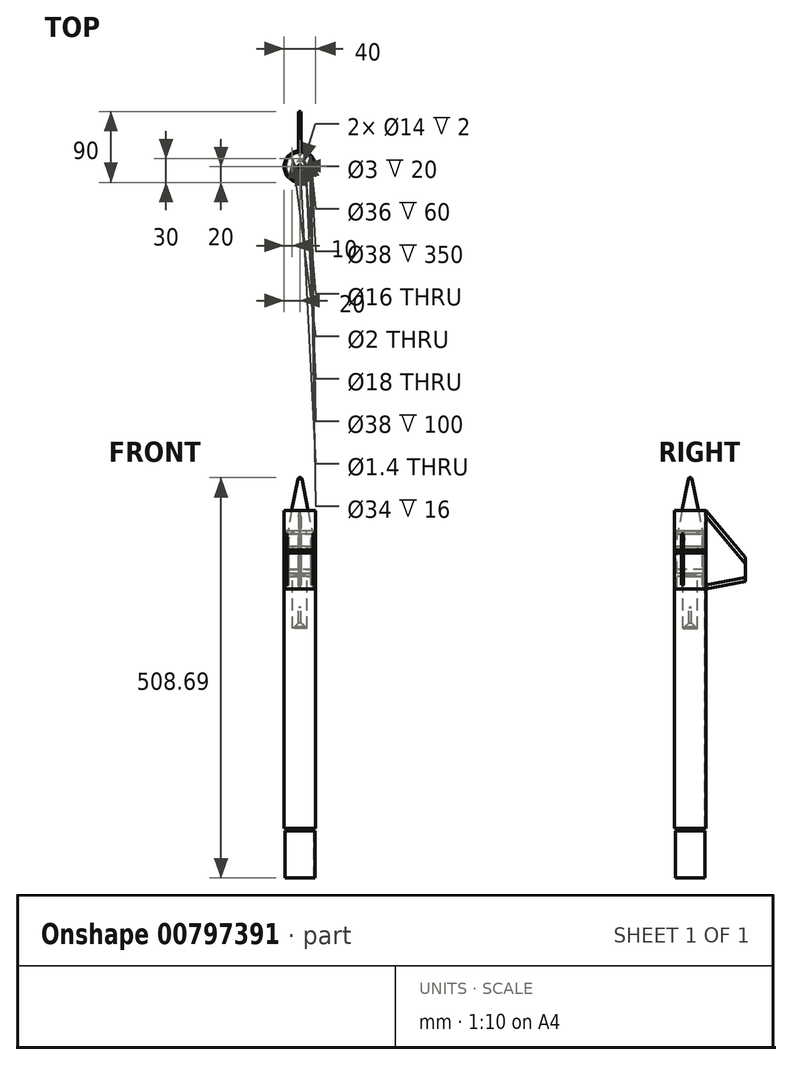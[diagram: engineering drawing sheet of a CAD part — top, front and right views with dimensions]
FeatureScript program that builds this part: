
annotation { "Feature Type Name" : "Feature", "Feature Type Description" : "" }
export const myFeature = defineFeature(function(context is Context, id is Id, definition is map)
    precondition{}
    {
        {
            var Q0;
            Q0=qCreatedBy(makeId("Front.planeOp"),FACE);
            var sketch = newSketch(context, id + "F0", { "sketchPlane" : qUnion([Q0])});
            skLineSegment(sketch, "E0", {"start": v(0, -25) * mm, "end": v(19, -25) * mm});
            skLineSegment(sketch, "E1", {"start": v(19, -25) * mm, "end": v(19, 0) * mm});
            skLineSegment(sketch, "E2", {"start": v(19, 0) * mm, "end": v(20, 0) * mm});
            skLineSegment(sketch, "E3", {"start": v(20, 0) * mm, "end": v(2.5, 90) * mm});
            skLineSegment(sketch, "E4", {"start": v(0, -25) * mm, "end": v(0, 89) * mm, "construction": true});
            skArc(sketch, "E5", {"start": v(2.5, 90) * mm, "mid": v(1.5, 91.23) * mm, "end": v(0, 91.7) * mm});
            skLineSegment(sketch, "E6", {"start": v(0, 91.7) * mm, "end": v(0, -25) * mm});
            skSolve(sketch);
        }
        {
            var Q0;
            Q0=makeQuery(id+"F0.imprint","IMPRINT",FACE,{"disambiguationData":[TD([[makeQuery(id+"F0.imprint","IMPRINT",EDGE,{"derivedFrom":sQuery(id+"F0.wireOp",EDGE,"E0")}),1.0]])]});
            var Q1;
            Q1=sQuery(id+"F0.wireOp",EDGE,"E6");
            revolve(context, id + "F1", {"surfaceOperationType" : NewSurfaceOperationType.NEW, "entities" : qUnion([Q0]), "axis" : qUnion([Q1]), "revolveType" : RevolveType.FULL});
        }
        {
            var Q0;
            Q0=qCreatedBy(makeId("Front.planeOp"),FACE);
            var sketch = newSketch(context, id + "F2", { "sketchPlane" : qUnion([Q0])});
            skLineSegment(sketch, "E7.bottom", {"start": v(19, -4) * mm, "end": v(20, -4) * mm});
            skLineSegment(sketch, "E7.top", {"start": v(19, -354) * mm, "end": v(20, -354) * mm});
            skLineSegment(sketch, "E7.left", {"start": v(19, -4) * mm, "end": v(19, -354) * mm});
            skLineSegment(sketch, "E7.right", {"start": v(20, -4) * mm, "end": v(20, -354) * mm});
            skLineSegment(sketch, "E8", {"start": v(0, 0) * mm, "end": v(0, -354) * mm, "construction": true});
            skSolve(sketch);
        }
        {
            var Q0;
            Q0=makeQuery(id+"F2.imprint","IMPRINT",FACE,{"disambiguationData":[TD([[makeQuery(id+"F2.imprint","IMPRINT",EDGE,{"derivedFrom":sQuery(id+"F2.wireOp",EDGE,"E7.bottom")}),-1.0]])]});
            var Q1;
            Q1=sQuery(id+"F2.wireOp",EDGE,"E8");
            revolve(context, id + "F3", {"surfaceOperationType" : NewSurfaceOperationType.NEW, "entities" : qUnion([Q0]), "axis" : qUnion([Q1]), "revolveType" : RevolveType.FULL});
        }
        {
            var Q0;
            Q0=qCreatedBy(makeId("Front.planeOp"),FACE);
            var sketch = newSketch(context, id + "F4", { "sketchPlane" : qUnion([Q0])});
            skLineSegment(sketch, "E9.bottom", {"start": v(18, -357) * mm, "end": v(19, -357) * mm});
            skLineSegment(sketch, "E9.top", {"start": v(18, -417) * mm, "end": v(19, -417) * mm});
            skLineSegment(sketch, "E9.left", {"start": v(18, -357) * mm, "end": v(18, -417) * mm});
            skLineSegment(sketch, "E9.right", {"start": v(19, -357) * mm, "end": v(19, -417) * mm});
            skLineSegment(sketch, "E10", {"start": v(0, 0) * mm, "end": v(0, -683.2) * mm, "construction": true});
            skSolve(sketch);
        }
        {
            var Q0;
            Q0=makeQuery(id+"F4.imprint","IMPRINT",FACE,{"disambiguationData":[TD([[makeQuery(id+"F4.imprint","IMPRINT",EDGE,{"derivedFrom":sQuery(id+"F4.wireOp",EDGE,"E9.bottom")}),-1.0]])]});
            var Q1;
            Q1=sQuery(id+"F4.wireOp",EDGE,"E10");
            revolve(context, id + "F5", {"surfaceOperationType" : NewSurfaceOperationType.NEW, "entities" : qUnion([Q0]), "axis" : qUnion([Q1]), "revolveType" : RevolveType.FULL});
        }
        {
            var Q0;
            Q0=qCreatedBy(makeId("Front.planeOp"),FACE);
            var sketch = newSketch(context, id + "F6", { "sketchPlane" : qUnion([Q0])});
            skLineSegment(sketch, "E11", {"start": v(0, 0) * mm, "end": v(0, -100) * mm, "construction": true});
            skLineSegment(sketch, "E12", {"start": v(17, 0) * mm, "end": v(18, 0) * mm});
            skLineSegment(sketch, "E13", {"start": v(18, 0) * mm, "end": v(18, -50) * mm});
            skLineSegment(sketch, "E14", {"start": v(18, -50) * mm, "end": v(17, -50) * mm});
            skLineSegment(sketch, "E15", {"start": v(17, -50) * mm, "end": v(17, -34) * mm});
            skLineSegment(sketch, "E16", {"start": v(17, -34) * mm, "end": v(0.7, -34) * mm});
            skLineSegment(sketch, "E17", {"start": v(0.7, -34) * mm, "end": v(0.7, -30) * mm});
            skLineSegment(sketch, "E18", {"start": v(0.7, -30) * mm, "end": v(17, -30) * mm});
            skLineSegment(sketch, "E19", {"start": v(17, -30) * mm, "end": v(17, 0) * mm});
            skSolve(sketch);
        }
        {
            var Q0;
            Q0=makeQuery(id+"F6.imprint","IMPRINT",FACE,{"disambiguationData":[TD([[makeQuery(id+"F6.imprint","IMPRINT",EDGE,{"derivedFrom":sQuery(id+"F6.wireOp",EDGE,"E12")}),-1.0]])]});
            var Q1;
            Q1=sQuery(id+"F6.wireOp",EDGE,"E11");
            revolve(context, id + "F7", {"surfaceOperationType" : NewSurfaceOperationType.NEW, "entities" : qUnion([Q0]), "axis" : qUnion([Q1]), "revolveType" : RevolveType.FULL});
        }
        {
            var Q0;
            Q0=qCreatedBy(makeId("Front.planeOp"),FACE);
            var sketch = newSketch(context, id + "F8", { "sketchPlane" : qUnion([Q0])});
            skLineSegment(sketch, "E20.bottom", {"start": v(20, 50) * mm, "end": v(19, 50) * mm});
            skLineSegment(sketch, "E20.top", {"start": v(20, -50) * mm, "end": v(19, -50) * mm});
            skLineSegment(sketch, "E20.left", {"start": v(20, 50) * mm, "end": v(20, -50) * mm});
            skLineSegment(sketch, "E20.right", {"start": v(19, 50) * mm, "end": v(19, -50) * mm});
            skLineSegment(sketch, "E21", {"start": v(0, 55) * mm, "end": v(0, -55) * mm, "construction": true});
            skSolve(sketch);
        }
        {
            var Q0;
            Q0=makeQuery(id+"F8.imprint","IMPRINT",FACE,{"disambiguationData":[TD([[makeQuery(id+"F8.imprint","IMPRINT",EDGE,{"derivedFrom":sQuery(id+"F8.wireOp",EDGE,"E20.bottom")}),1.0]])]});
            var Q1;
            Q1=sQuery(id+"F8.wireOp",EDGE,"E21");
            revolve(context, id + "F9", {"surfaceOperationType" : NewSurfaceOperationType.NEW, "entities" : qUnion([Q0]), "axis" : qUnion([Q1]), "revolveType" : RevolveType.FULL});
        }
        {
            var Q0;
            Q0=qCreatedBy(makeId("Top.planeOp"),FACE);
            cPlane(context, id + "F10", {"entities" : qUnion([Q0]), "cplaneType" : CPlaneType.OFFSET, "offset" : 20 * mm, "width" : 150 * mm, "height" : 150 * mm});
        }
        {
            var Q0;
            Q0=qCreatedBy(id+"F10.planeOp",FACE);
            var sketch = newSketch(context, id + "F11", { "sketchPlane" : qUnion([Q0])});
            skLineSegment(sketch, "E22.bottom", {"start": v(-1.5, 21.95) * mm, "end": v(1.5, 21.95) * mm});
            skLineSegment(sketch, "E22.top", {"start": v(-1.5, 16.95) * mm, "end": v(1.5, 16.95) * mm});
            skLineSegment(sketch, "E22.left", {"start": v(-1.5, 21.95) * mm, "end": v(-1.5, 16.95) * mm});
            skLineSegment(sketch, "E22.right", {"start": v(1.5, 21.95) * mm, "end": v(1.5, 16.95) * mm});
            skLineSegment(sketch, "E23.1.0", {"start": v(-18.26, -12.27) * mm, "end": v(-19.76, -9.68) * mm});
            skLineSegment(sketch, "E23.1.1", {"start": v(-18.26, -12.27) * mm, "end": v(-13.93, -9.77) * mm});
            skLineSegment(sketch, "E23.2.0", {"start": v(19.76, -9.68) * mm, "end": v(18.26, -12.27) * mm});
            skLineSegment(sketch, "E23.2.1", {"start": v(19.76, -9.68) * mm, "end": v(15.43, -7.18) * mm});
            skPoint(sketch, "E23.center", {"position": v(0, 0) * mm});
            skLineSegment(sketch, "E24.1.0", {"start": v(-19.76, -9.68) * mm, "end": v(-15.43, -7.18) * mm});
            skLineSegment(sketch, "E24.1.1", {"start": v(-13.93, -9.77) * mm, "end": v(-15.43, -7.18) * mm});
            skLineSegment(sketch, "E24.2.0", {"start": v(18.26, -12.27) * mm, "end": v(13.93, -9.77) * mm});
            skLineSegment(sketch, "E24.2.1", {"start": v(15.43, -7.18) * mm, "end": v(13.93, -9.77) * mm});
            skSolve(sketch);
        }
        {
            var Q0;
            Q0=makeQuery(id+"F11.imprint","IMPRINT",FACE,{"disambiguationData":[TD([[makeQuery(id+"F11.imprint","IMPRINT",EDGE,{"derivedFrom":sQuery(id+"F11.wireOp",EDGE,"E24.1.0")}),-1.0]])]});
            var Q1;
            Q1=makeQuery(id+"F11.imprint","IMPRINT",FACE,{"disambiguationData":[TD([[makeQuery(id+"F11.imprint","IMPRINT",EDGE,{"derivedFrom":sQuery(id+"F11.wireOp",EDGE,"E24.2.0")}),-1.0]])]});
            var Q2;
            Q2=makeQuery(id+"F11.imprint","IMPRINT",FACE,{"disambiguationData":[TD([[makeQuery(id+"F11.imprint","IMPRINT",EDGE,{"derivedFrom":sQuery(id+"F11.wireOp",EDGE,"E22.bottom")}),-1.0]])]});
            extrude(context, id + "F12", {"entities" : qUnion([Q0, Q1, Q2]), "operationType" : NewBodyOperationType.REMOVE, "depth" : -65 * mm, "offsetDistance" : 25 * mm});
        }
        {
            var Q0;
            Q0=qCreatedBy(makeId("Right.planeOp"),FACE);
            var sketch = newSketch(context, id + "F13", { "sketchPlane" : qUnion([Q0])});
            skLineSegment(sketch, "E25", {"start": v(20, 50) * mm, "end": v(70, -10) * mm});
            skLineSegment(sketch, "E26", {"start": v(70, -10) * mm, "end": v(70, -40) * mm});
            skLineSegment(sketch, "E27", {"start": v(70, -40) * mm, "end": v(20, -50) * mm});
            skLineSegment(sketch, "E28", {"start": v(20, -50) * mm, "end": v(20, -45) * mm});
            skLineSegment(sketch, "E29", {"start": v(20, -45) * mm, "end": v(15, -45) * mm});
            skLineSegment(sketch, "E30", {"start": v(20, 50) * mm, "end": v(20, 16) * mm});
            skLineSegment(sketch, "E31", {"start": v(20, 16) * mm, "end": v(15, 16) * mm});
            skLineSegment(sketch, "E32", {"start": v(15, 16) * mm, "end": v(15, -45) * mm});
            skSolve(sketch);
        }
        {
            var Q0;
            Q0=makeQuery(id+"F13.imprint","IMPRINT",FACE,{"disambiguationData":[TD([[makeQuery(id+"F13.imprint","IMPRINT",EDGE,{"derivedFrom":sQuery(id+"F13.wireOp",EDGE,"E25")}),-1.0]])]});
            extrude(context, id + "F14", {"entities" : qUnion([Q0]), "endBound" : BoundingType.SYMMETRIC, "oppositeDirection" : true, "depth" : 3 * mm, "offsetDistance" : 25 * mm});
        }
        {
            var Q0;
            Q0=makeQuery(id+"F14.opExtrude","CAP_EDGE",EDGE,{"disambiguationData":[OSD([sQuery(id+"F13.wireOp",EDGE,"E25")])],"isStart":true});
            var Q1;
            Q1=makeQuery(id+"F14.opExtrude","CAP_EDGE",EDGE,{"disambiguationData":[OSD([sQuery(id+"F13.wireOp",EDGE,"E25")])],"isStart":false});
            var Q2;
            Q2=makeQuery(id+"F14.opExtrude","CAP_EDGE",EDGE,{"disambiguationData":[OSD([sQuery(id+"F13.wireOp",EDGE,"E27")])],"isStart":true});
            chamfer(context, id + "F15", {"entities" : qUnion([Q0, Q1, Q2]), "chamferType" : ChamferType.TWO_OFFSETS, "width1" : 1 * mm, "oppositeDirection" : false, "width2" : 5 * mm, "tangentPropagation" : true});
        }
        {
            var Q0;
            Q0=makeQuery(id+"F14.opExtrude","CAP_EDGE",EDGE,{"disambiguationData":[OSD([sQuery(id+"F13.wireOp",EDGE,"E27")])],"isStart":false});
            chamfer(context, id + "F16", {"entities" : qUnion([Q0]), "chamferType" : ChamferType.TWO_OFFSETS, "width1" : 5 * mm, "oppositeDirection" : false, "width2" : 1 * mm, "tangentPropagation" : true});
        }
        {
            var Q0;
            Q0=qCreatedBy(makeId("Top.planeOp"),FACE);
            var sketch = newSketch(context, id + "F17", { "sketchPlane" : qUnion([Q0])});
            skCircle(sketch, "E33", {"center": v(0, 0) * mm, "radius": 9 * mm});
            skCircle(sketch, "E34", {"center": v(0, 0) * mm, "radius": 19 * mm});
            skSolve(sketch);
        }
        {
            var Q0;
            Q0=makeQuery(id+"F17.imprint","IMPRINT",FACE,{"disambiguationData":[TD([[makeQuery(id+"F17.imprint","IMPRINT",EDGE,{"derivedFrom":sQuery(id+"F17.wireOp",EDGE,"E33")}),-1.0]])]});
            extrude(context, id + "F18", {"entities" : qUnion([Q0]), "depth" : 4 * mm, "offsetDistance" : 25 * mm});
        }
        {
            var Q0;
            Q0=qCreatedBy(id+"F10.planeOp",FACE);
            var sketch = newSketch(context, id + "F19", { "sketchPlane" : qUnion([Q0])});
            skCircle(sketch, "E35", {"center": v(0, 0) * mm, "radius": 19 * mm});
            skCircle(sketch, "E36", {"center": v(0, 0) * mm, "radius": 8 * mm});
            skCircle(sketch, "E37", {"center": v(-10, 10) * mm, "radius": 1 * mm});
            skSolve(sketch);
        }
        {
            var Q0;
            Q0=makeQuery(id+"F19.imprint","IMPRINT",FACE,{"disambiguationData":[TD([[makeQuery(id+"F19.imprint","IMPRINT",EDGE,{"derivedFrom":sQuery(id+"F19.wireOp",EDGE,"E35")}),1.0]])]});
            extrude(context, id + "F20", {"entities" : qUnion([Q0]), "depth" : 4 * mm, "offsetDistance" : 25 * mm});
        }
        {
            var Q0;
            Q0=qCreatedBy(makeId("Front.planeOp"),FACE);
            var sketch = newSketch(context, id + "F21", { "sketchPlane" : qUnion([Q0])});
            skLineSegment(sketch, "E38", {"start": v(0, -32) * mm, "end": v(7, -32) * mm});
            skLineSegment(sketch, "E39", {"start": v(7, -32) * mm, "end": v(7, -30) * mm});
            skLineSegment(sketch, "E40", {"start": v(7, -30) * mm, "end": v(9, -30) * mm});
            skLineSegment(sketch, "E41", {"start": v(9, -30) * mm, "end": v(9, -100) * mm});
            skLineSegment(sketch, "E42", {"start": v(9, -100) * mm, "end": v(7, -100) * mm});
            skLineSegment(sketch, "E43", {"start": v(7, -100) * mm, "end": v(7, -98) * mm});
            skLineSegment(sketch, "E44", {"start": v(7, -98) * mm, "end": v(1.5, -93) * mm});
            skLineSegment(sketch, "E45", {"start": v(1.5, -93) * mm, "end": v(1.5, -73) * mm});
            skLineSegment(sketch, "E46", {"start": v(1.5, -73) * mm, "end": v(0, -73) * mm});
            skLineSegment(sketch, "E47", {"start": v(0, -73) * mm, "end": v(0, -32) * mm});
            skLineSegment(sketch, "E48", {"start": v(0, 0) * mm, "end": v(0, -130) * mm, "construction": true});
            skSolve(sketch);
        }
        {
            var Q0;
            Q0=makeQuery(id+"F21.imprint","IMPRINT",FACE,{"disambiguationData":[TD([[makeQuery(id+"F21.imprint","IMPRINT",EDGE,{"derivedFrom":sQuery(id+"F21.wireOp",EDGE,"E38")}),-1.0]])]});
            var Q1;
            Q1=sQuery(id+"F21.wireOp",EDGE,"E48");
            revolve(context, id + "F22", {"surfaceOperationType" : NewSurfaceOperationType.NEW, "entities" : qUnion([Q0]), "axis" : qUnion([Q1]), "revolveType" : RevolveType.FULL});
        }
    });
